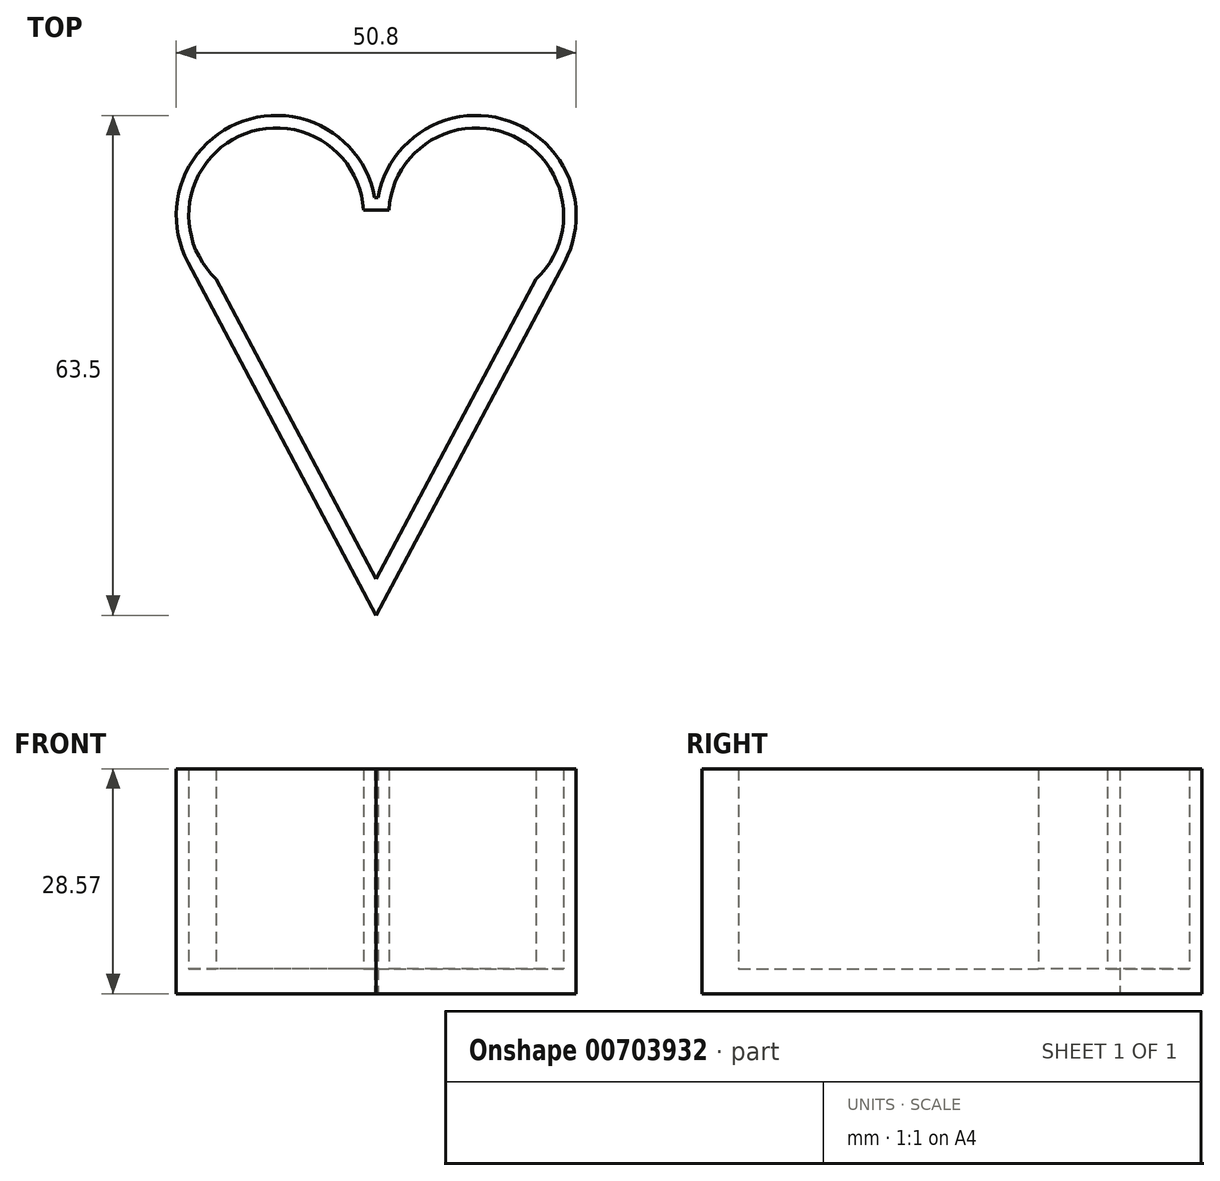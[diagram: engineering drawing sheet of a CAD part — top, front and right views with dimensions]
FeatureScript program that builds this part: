
annotation { "Feature Type Name" : "Feature", "Feature Type Description" : "" }
export const myFeature = defineFeature(function(context is Context, id is Id, definition is map)
    precondition{}
    {
        {
            var Q0;
            Q0=qCreatedBy(makeId("Top.planeOp"),FACE);
            var sketch = newSketch(context, id + "F0", { "sketchPlane" : qUnion([Q0])});
            skArc(sketch, "E0", {"start": v(-0.2, 53.07) * mm, "mid": v(-16.88, 62.8) * mm, "end": v(-23.9, 44.82) * mm});
            skArc(sketch, "E1", {"start": v(23.9, 44.82) * mm, "mid": v(16.88, 62.8) * mm, "end": v(0.2, 53.07) * mm});
            skLineSegment(sketch, "E2", {"start": v(-23.9, 44.82) * mm, "end": v(0, 0) * mm});
            skLineSegment(sketch, "E3", {"start": v(23.9, 44.82) * mm, "end": v(0, 0) * mm});
            skLineSegment(sketch, "E4", {"start": v(0.2, 53.07) * mm, "end": v(-0.2, 53.07) * mm});
            skSolve(sketch);
        }
        {
            var Q0;
            Q0 = qSketchRegion(id + "F0", true);
            extrude(context, id + "F1", {"entities" : qUnion([Q0]), "depth" : 3.17 * mm, "offsetDistance" : 25.4 * mm});
        }
        {
            var Q0;
            Q0=makeQuery(id+"F1.opExtrude","CAP_FACE",FACE,{"disambiguationData":[OSD([sQuery(id+"F0.wireOp",EDGE,"E0"),sQuery(id+"F0.wireOp",EDGE,"E1"),sQuery(id+"F0.wireOp",EDGE,"E2"),sQuery(id+"F0.wireOp",EDGE,"E3"),sQuery(id+"F0.wireOp",EDGE,"E4")])],"isStart":false});
            var sketch = newSketch(context, id + "F2", { "sketchPlane" : qUnion([Q0])});
            skArc(sketch, "E5", {"start": v(-1.6, 51.49) * mm, "mid": v(-17.42, 60.86) * mm, "end": v(-20.32, 42.7) * mm});
            skArc(sketch, "E6", {"start": v(20.32, 42.7) * mm, "mid": v(17.42, 60.86) * mm, "end": v(1.6, 51.49) * mm});
            skLineSegment(sketch, "E7", {"start": v(0, 4.62) * mm, "end": v(20.32, 42.7) * mm});
            skLineSegment(sketch, "E8", {"start": v(0, 4.62) * mm, "end": v(-20.32, 42.7) * mm});
            skLineSegment(sketch, "E9", {"start": v(-1.6, 51.49) * mm, "end": v(1.6, 51.49) * mm});
            skSolve(sketch);
        }
        {
            var Q0;
            Q0=makeQuery(id+"F2.imprint","IMPRINT",FACE,{"disambiguationData":[TD([[makeQuery(id+"F2.imprint","IMPRINT",EDGE,{"derivedFrom":sQuery(id+"F2.wireOp",EDGE,"E5")}),-1.0]])]});
            extrude(context, id + "F3", {"entities" : qUnion([Q0]), "operationType" : NewBodyOperationType.ADD, "depth" : 25.4 * mm, "offsetDistance" : 25.4 * mm});
        }
    });
